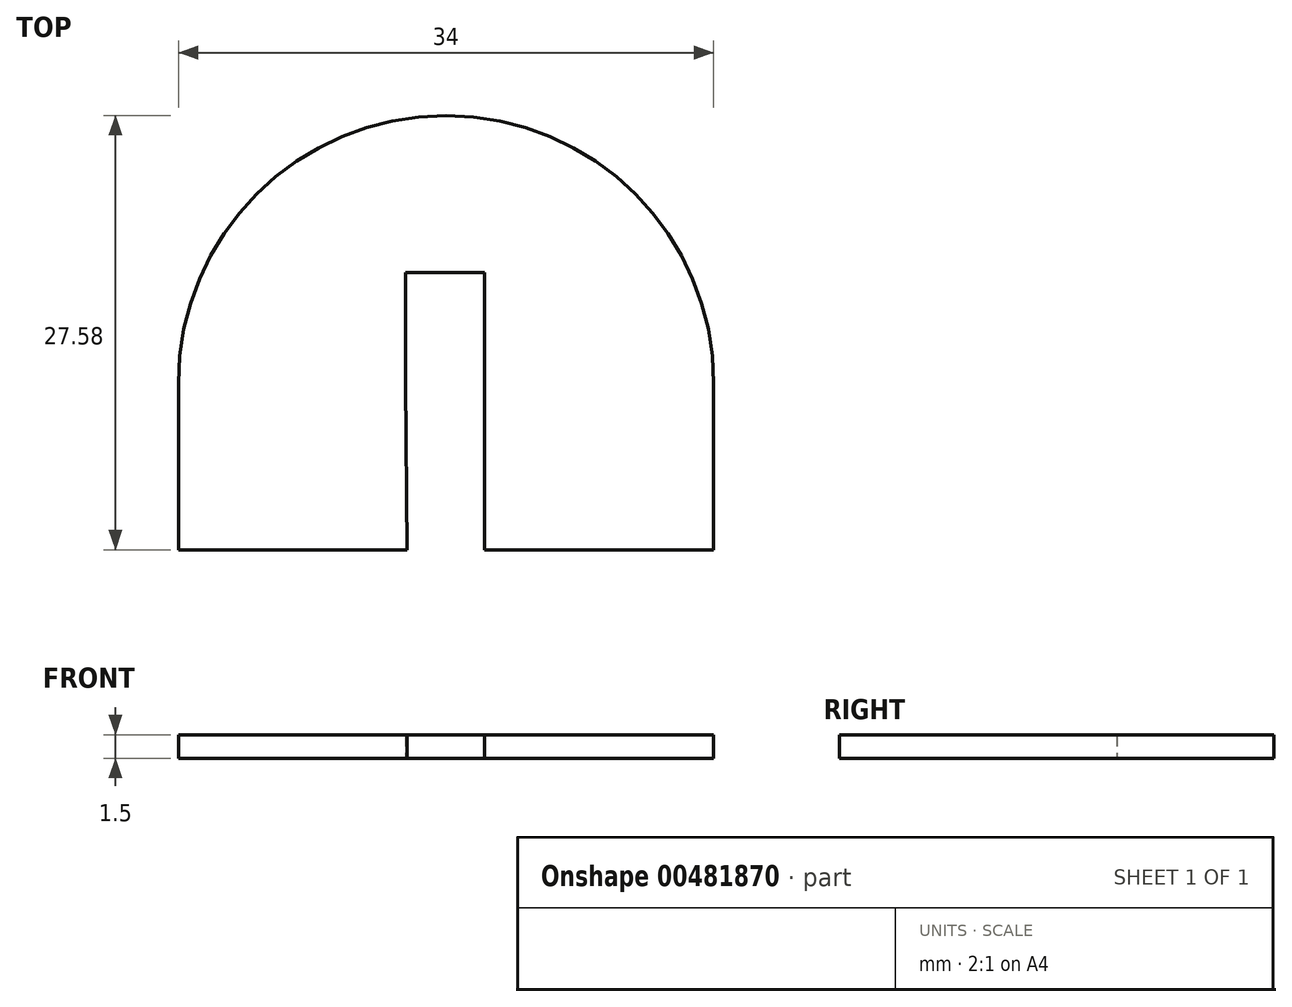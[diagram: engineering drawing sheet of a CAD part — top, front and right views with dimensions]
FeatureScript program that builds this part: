
annotation { "Feature Type Name" : "Feature", "Feature Type Description" : "" }
export const myFeature = defineFeature(function(context is Context, id is Id, definition is map)
    precondition{}
    {
        {
            var Q0;
            Q0=qCreatedBy(makeId("Top.planeOp"),FACE);
            var sketch = newSketch(context, id + "F0", { "sketchPlane" : qUnion([Q0])});
            skArc(sketch, "E0", {"start": v(17.48, -5.1) * mm, "mid": v(0.48, 11.9) * mm, "end": v(-16.52, -5.1) * mm});
            skPoint(sketch, "E1", {"position": v(-2.08, 1.9) * mm});
            skPoint(sketch, "E2", {"position": v(2.92, 1.9) * mm});
            skPoint(sketch, "E3", {"position": v(0.42, 1.9) * mm});
            skPoint(sketch, "E4", {"position": v(-2.08, -5.1) * mm});
            skPoint(sketch, "E5", {"position": v(2.92, -5.1) * mm});
            skPoint(sketch, "E6", {"position": v(-16.52, -15.7) * mm});
            skPoint(sketch, "E7", {"position": v(17.48, -15.7) * mm});
            skLineSegment(sketch, "E8", {"start": v(-2.08, -5.1) * mm, "end": v(-2.08, 1.9) * mm});
            skLineSegment(sketch, "E9", {"start": v(2.92, 1.9) * mm, "end": v(0.42, 1.9) * mm});
            skLineSegment(sketch, "E10", {"start": v(0.42, 1.9) * mm, "end": v(-2.08, 1.9) * mm});
            skLineSegment(sketch, "E11", {"start": v(2.92, 1.9) * mm, "end": v(2.92, -5.1) * mm});
            skLineSegment(sketch, "E12.left", {"start": v(-16.52, -15.7) * mm, "end": v(-16.52, -5.1) * mm});
            skLineSegment(sketch, "E12.right", {"start": v(17.48, -15.7) * mm, "end": v(17.48, -5.1) * mm});
            skLineSegment(sketch, "E13", {"start": v(-16.52, -15.7) * mm, "end": v(-2, -15.7) * mm});
            skPoint(sketch, "E14", {"position": v(-2, -15.7) * mm});
            skPoint(sketch, "E15", {"position": v(2.92, -15.7) * mm});
            skLineSegment(sketch, "E16", {"start": v(-2.08, -5.1) * mm, "end": v(-2, -15.7) * mm});
            skLineSegment(sketch, "E17", {"start": v(2.92, -5.1) * mm, "end": v(2.92, -15.7) * mm});
            skLineSegment(sketch, "E18.trimOffspring", {"start": v(2.92, -15.7) * mm, "end": v(17.48, -15.7) * mm});
            skSolve(sketch);
        }
        {
            var Q0;
            Q0=makeQuery(id+"F0.imprint","IMPRINT",FACE,{"disambiguationData":[TD([[makeQuery(id+"F0.imprint","IMPRINT",EDGE,{"derivedFrom":sQuery(id+"F0.wireOp",EDGE,"E0")}),1.0]])]});
            extrude(context, id + "F1", {"entities" : qUnion([Q0]), "depth" : 1.5 * mm});
        }
    });
